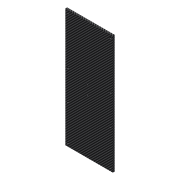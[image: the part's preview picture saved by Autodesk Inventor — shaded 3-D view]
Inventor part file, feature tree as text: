
AUTODESK INVENTOR PART (.ipt)
format: ipt  version: 2018 (Build 220112000, 112)  size: 163,840 bytes
history: native  units: mm
features: other x4, extrude x3, sketch x2, reference x2
ambient origin geometry x8: Origin, YZ Plane, XZ Plane, XY Plane, X Axis, Y Axis, Z Axis, Center Point
bodies: Volumenkörper1 (feature_tree)
feature tree (11):
  sketch  "Skizze1"  dims[d1=40.0mm d2=40.0mm]
  extrude  "Extrusion1"  Depth=40.0mm
  extrude  "Extrusion2"  Depth=10.0mm
  extrude  "Extrusion3"  Depth=3.0mm TaperAngle=0.0deg
  sketch  "Skizze2"  dims[d3=100.0mm d4=100.0mm d5=3.0mm d6=0.0mm d7=3.4mm d8=4.0mm d9=5.0mm d10=3.4mm d11=4.0mm d12=5.0mm d13=3.4mm d14=4.0mm d15=5.0mm d16=3.4mm d17=5.0mm d18=4.0mm d19=10.0mm d20=0.0mm d21=10.0mm d22=0.0mm d23=800.0mm d25=80.0mm d26=10.0mm d28=10.0mm d30=20.0mm d32=50.0mm d33=10.0mm d35=10.0mm]
  reference  "Referenz1"
  reference  "Referenz2"
  other  "<userpath>\OneDrive\Development\RTW\03_Konstruktion\Mohne komplett.iam"
  other  "Mohne komplett.iam"
  other  "MPU 6050 IMU:1"
  other  "Base:1"
